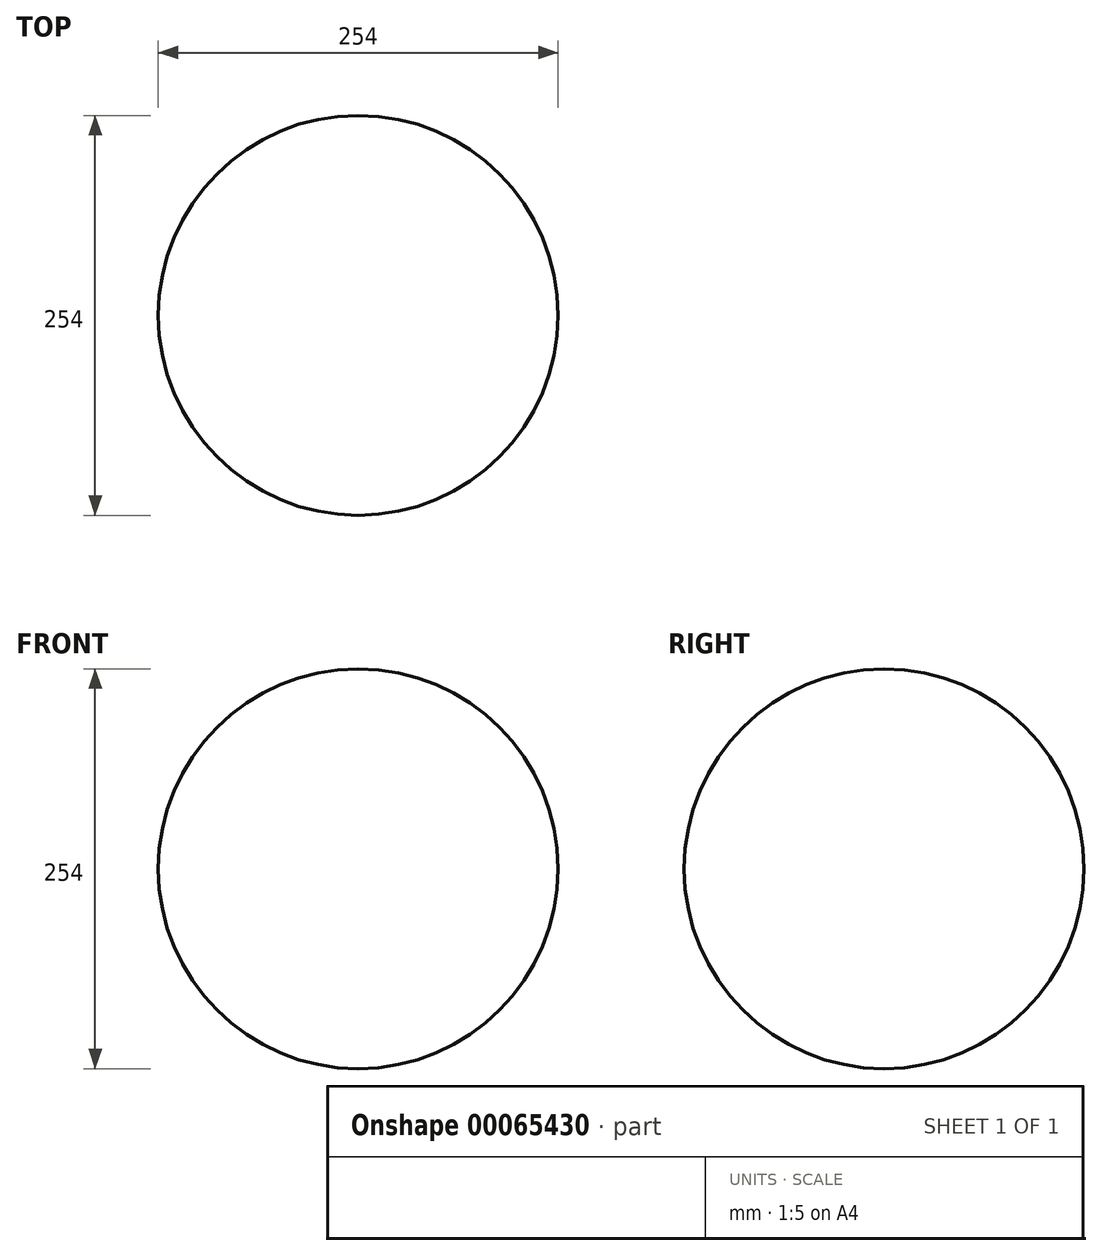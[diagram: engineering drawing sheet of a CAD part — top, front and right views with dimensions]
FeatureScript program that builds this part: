
annotation { "Feature Type Name" : "Feature", "Feature Type Description" : "" }
export const myFeature = defineFeature(function(context is Context, id is Id, definition is map)
    precondition{}
    {
        {
            var Q0;
            Q0=qCreatedBy(makeId("Front.planeOp"),FACE);
            var sketch = newSketch(context, id + "F0", { "sketchPlane" : qUnion([Q0])});
            skArc(sketch, "E0", {"start": v(0, 254) * mm, "mid": v(-127, 127) * mm, "end": v(0, 0) * mm});
            skLineSegment(sketch, "E1", {"start": v(0, 254) * mm, "end": v(0, 0) * mm});
            skSolve(sketch);
        }
        {
            var Q0;
            Q0=makeQuery(id+"F0.imprint","IMPRINT",FACE,{"disambiguationData":[TD([[makeQuery(id+"F0.imprint","IMPRINT",EDGE,{"derivedFrom":sQuery(id+"F0.wireOp",EDGE,"E0")}),1.0]])]});
            var Q1;
            Q1=sQuery(id+"F0.wireOp",EDGE,"E1");
            revolve(context, id + "F1", {"entities" : qUnion([Q0]), "axis" : qUnion([Q1]), "revolveType" : RevolveType.FULL});
        }
    });
